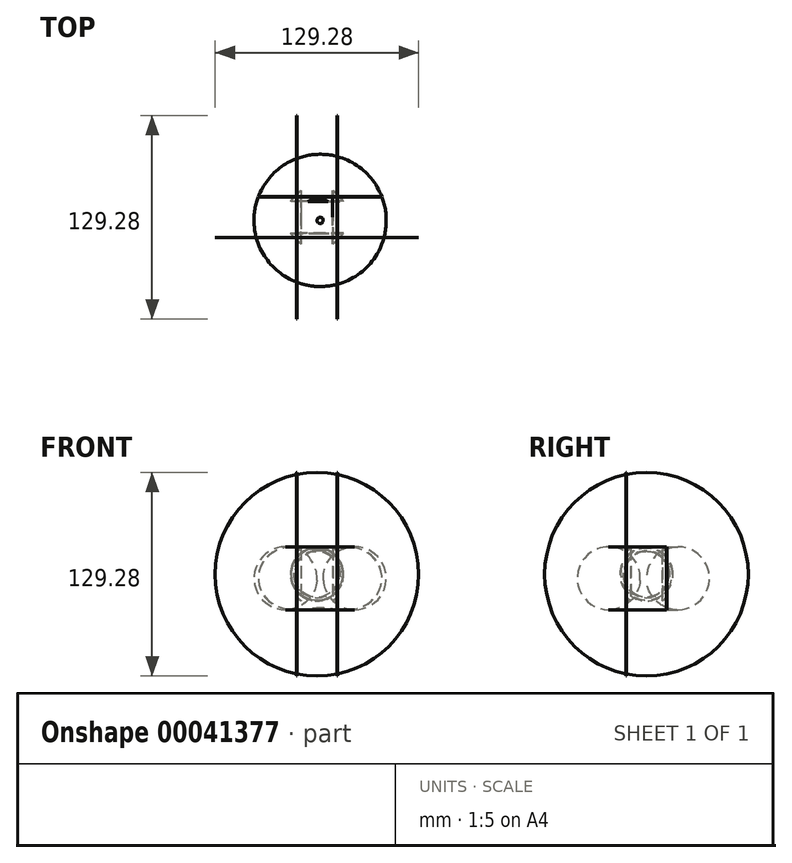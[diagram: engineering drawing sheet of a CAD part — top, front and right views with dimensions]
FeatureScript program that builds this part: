
annotation { "Feature Type Name" : "Feature", "Feature Type Description" : "" }
export const myFeature = defineFeature(function(context is Context, id is Id, definition is map)
    precondition{}
    {
        {
            var Q0;
            Q0=qCreatedBy(makeId("Front.planeOp"),FACE);
            cPlane(context, id + "F0", {"entities" : qUnion([Q0]), "cplaneType" : CPlaneType.OFFSET, "offset" : 2 * mm, "width" : 150 * mm, "height" : 150 * mm});
        }
        {
            var Q0;
            Q0=qCreatedBy(id+"F0.planeOp",FACE);
            var sketch = newSketch(context, id + "F1", { "sketchPlane" : qUnion([Q0])});
            skLineSegment(sketch, "E0", {"start": v(2, 24) * mm, "end": v(2, -2.5) * mm});
            skLineSegment(sketch, "E1", {"start": v(2, -2.5) * mm, "end": v(24, -2.5) * mm});
            skCircle(sketch, "E2", {"center": v(24, -2.5) * mm, "radius": 20 * mm});
            skLineSegment(sketch, "E3", {"start": v(0, 0) * mm, "end": v(0, 14.59) * mm});
            skSolve(sketch);
        }
        {
            var Q0;
            Q0=makeQuery(id+"F1.imprint","IMPRINT",FACE,{"disambiguationData":[TD([[makeQuery(id+"F1.imprint","IMPRINT",EDGE,{"derivedFrom":sQuery(id+"F1.wireOp",EDGE,"E2")}),1.0]])]});
            var Q1;
            Q1=sQuery(id+"F1.wireOp",EDGE,"E0");
            revolve(context, id + "F2", {"entities" : qUnion([Q0]), "axis" : qUnion([Q1]), "revolveType" : RevolveType.FULL});
        }
        {
            var Q0;
            Q0=qCreatedBy(makeId("Front.planeOp"),FACE);
            var sketch = newSketch(context, id + "F3", { "sketchPlane" : qUnion([Q0])});
            skLineSegment(sketch, "E4", {"start": v(10.25, 0) * mm, "end": v(10.25, 16.43) * mm});
            skLineSegment(sketch, "E5", {"start": v(13, 14.35) * mm, "end": v(13, 64.64) * mm});
            skArc(sketch, "E6", {"start": v(13, 14.35) * mm, "mid": v(11.67, 15.45) * mm, "end": v(10.25, 16.43) * mm});
            skLineSegment(sketch, "E7.0", {"start": v(12.75, 14.9) * mm, "end": v(12.75, 64.64) * mm});
            skArc(sketch, "E7.1", {"start": v(12.75, 14.9) * mm, "mid": v(11.42, 15.95) * mm, "end": v(10, 16.88) * mm});
            skLineSegment(sketch, "E7.2", {"start": v(10, 0) * mm, "end": v(10, 16.88) * mm});
            skLineSegment(sketch, "E8", {"start": v(12.75, 64.64) * mm, "end": v(13, 64.64) * mm});
            skLineSegment(sketch, "E9", {"start": v(10, 0) * mm, "end": v(10.25, 0) * mm});
            skLineSegment(sketch, "E10.bottom", {"start": v(0, 0) * mm, "end": v(20, 0) * mm, "construction": true});
            skLineSegment(sketch, "E10.top", {"start": v(0, 28.2) * mm, "end": v(20, 28.2) * mm, "construction": true});
            skLineSegment(sketch, "E10.left", {"start": v(0, 0) * mm, "end": v(0, 28.2) * mm, "construction": true});
            skLineSegment(sketch, "E10.right", {"start": v(20, 0) * mm, "end": v(20, 28.2) * mm, "construction": true});
            skLineSegment(sketch, "E11", {"start": v(0, 0) * mm, "end": v(20, 28.2) * mm, "construction": true});
            skLineSegment(sketch, "E12", {"start": v(0, 0) * mm, "end": v(20, 20) * mm, "construction": true});
            skSolve(sketch);
        }
        {
            var Q0;
            Q0=makeQuery(id+"F3.imprint","IMPRINT",FACE,{"disambiguationData":[TD([[makeQuery(id+"F3.imprint","IMPRINT",EDGE,{"derivedFrom":sQuery(id+"F3.wireOp",EDGE,"E4")}),1.0]])]});
            var Q1;
            Q1=sQuery(id+"F3.wireOp",EDGE,"E9");
            revolve(context, id + "F4", {"entities" : qUnion([Q0]), "axis" : qUnion([Q1]), "revolveType" : RevolveType.FULL});
        }
        {
            var Q0;
            Q0=qCreatedBy(makeId("Front.planeOp"),FACE);
            var sketch = newSketch(context, id + "F5", { "sketchPlane" : qUnion([Q0])});
            skLineSegment(sketch, "E13", {"start": v(0, 0) * mm, "end": v(0, 81.05) * mm});
            skSolve(sketch);
        }
        {
            var Q0;
            Q0=makeQuery(id+"F4.opRevolve","SWEPT_BODY",BODY,{"disambiguationData":[OSD([sQuery(id+"F3.wireOp",EDGE,"E4"),sQuery(id+"F3.wireOp",EDGE,"E5"),sQuery(id+"F3.wireOp",EDGE,"E6"),sQuery(id+"F3.wireOp",EDGE,"E7.0"),sQuery(id+"F3.wireOp",EDGE,"E7.1"),sQuery(id+"F3.wireOp",EDGE,"E7.2"),sQuery(id+"F3.wireOp",EDGE,"E8"),sQuery(id+"F3.wireOp",EDGE,"E9")])]});
            var Q1;
            Q1=sQuery(id+"F5.wireOp",EDGE,"E13");
            circularPattern(context, id + "F6", {"entities" : qUnion([Q0]), "axis" : qUnion([Q1]), "angle" : 90 * degree, "instanceCount" : 4});
        }
        {
            var Q0;
            Q0=makeQuery(id+"F6.opPattern","COPY",BODY,{"derivedFrom":makeQuery(id+"F4.opRevolve","SWEPT_BODY",BODY,{"disambiguationData":[OSD([sQuery(id+"F3.wireOp",EDGE,"E4"),sQuery(id+"F3.wireOp",EDGE,"E5"),sQuery(id+"F3.wireOp",EDGE,"E6"),sQuery(id+"F3.wireOp",EDGE,"E7.0"),sQuery(id+"F3.wireOp",EDGE,"E7.1"),sQuery(id+"F3.wireOp",EDGE,"E7.2"),sQuery(id+"F3.wireOp",EDGE,"E8"),sQuery(id+"F3.wireOp",EDGE,"E9")])]}),"instanceName":"1"});
            var Q1;
            Q1=makeQuery(id+"F2.opRevolve","SWEPT_BODY",BODY,{"disambiguationData":[OSD([sQuery(id+"F1.wireOp",EDGE,"E2")])]});
            booleanBodies(context, id + "F7", {"operationType" : BooleanOperationType.SUBTRACTION, "tools" : qUnion([Q0]), "targets" : qUnion([Q1])});
        }
    });
